FCSTD DOCUMENT  (FreeCAD 0.20R0.20.2)
Label: 002
License: All rights reserved
LicenseURL: http://en.wikipedia.org/wiki/All_rights_reserved
objects: Sketcher::SketchObject×1
note: 1 computed .brp shape members not serialized (recipe doc carries the construction recipe); baked Part::Feature solids carry a one-line shape summary decoded from their .brp

FEATURE [Sketcher::SketchObject] Sketch
  FullyConstrained = true
  sketch-geometry (9):
    g0: Circle CenterX=7 CenterY=0 CenterZ=0 NormalX=0 NormalY=0 NormalZ=1 AngleXU=0 Radius=2
    g1: Circle CenterX=0 CenterY=7 CenterZ=0 NormalX=0 NormalY=0 NormalZ=1 AngleXU=0 Radius=2
    g2: Circle CenterX=0 CenterY=0 CenterZ=0 NormalX=0 NormalY=0 NormalZ=1 AngleXU=0 Radius=2.8
    g3: Circle CenterX=-7 CenterY=0 CenterZ=0 NormalX=0 NormalY=0 NormalZ=1 AngleXU=0 Radius=2
    g4: Circle CenterX=0 CenterY=-7 CenterZ=0 NormalX=0 NormalY=0 NormalZ=1 AngleXU=0 Radius=2
    g5: LineSegment StartX=-18.75 StartY=10.5 StartZ=0 EndX=-18.75 EndY=-10.5 EndZ=0
    g6: LineSegment StartX=-18.75 StartY=10.5 StartZ=0 EndX=18.75 EndY=10.5 EndZ=0
    g7: LineSegment StartX=-18.75 StartY=-10.5 StartZ=0 EndX=18.75 EndY=-10.5 EndZ=0
    g8: LineSegment StartX=18.75 StartY=10.5 StartZ=0 EndX=18.75 EndY=-10.5 EndZ=0
  constraints (16):
    c: Block(g2)
    c: Block(g1)
    c: Block(g0)
    c: Block(g3)
    c: Block(g4)
    c: Vertical(g5)
    c: Block(g5)
    c: Coincident(g6,g5)
    c: Horizontal(g6)
    c: Coincident(g7,g5)
    c: Horizontal(g7)
    c: Block(g6)
    c: Block(g7)
    c: Coincident(g8,g6)
    c: Coincident(g8,g7)
    c: Vertical(g8)
